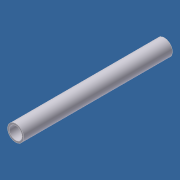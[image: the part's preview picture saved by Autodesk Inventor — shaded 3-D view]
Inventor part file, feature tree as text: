
AUTODESK INVENTOR PART (.ipt)
format: ipt  version: 2012 (Build 160160000, 160)  size: 82,432 bytes
history: native  units: in
note: dims shown in document units (in); Inventor stores cm internally (conversion verified against a paired STEP export)
features: extrude x2, sketch x2, plane x1, thread x1, other x1, projected_geometry x1
ambient origin geometry x8: Origin, YZ Plane, XZ Plane, XY Plane, X Axis, Y Axis, Z Axis, Center Point
bodies: Solid1 (feature_tree)
feature tree (8):
  extrude  "Extrusion1"  Depth=1.0313in
  plane  "Work Plane1"
  sketch  "Sketch2"  dims[d2=12.0in d3=0.0in d4=0.0in d5=0.25in d6=0.201in d7=5.5in d8=12.0in d9=0.0in d12=1.0in d13=0.0in]
  extrude  "Extrusion2"  TaperAngle=0.0deg  [1 undecoded]
  thread  "Thread1"  [1 undecoded]
  sketch  "Sketch1"  dims[d0=1.3125in d1=1.0313in]
  other  "Work Axis1"
  projected_geometry  "Projected Loop1"
note: 2 required parameter values undecoded (feature->parameter linkage not recoverable at this tier; creation-order binding heuristic only, values carry confidence <= 0.55)
